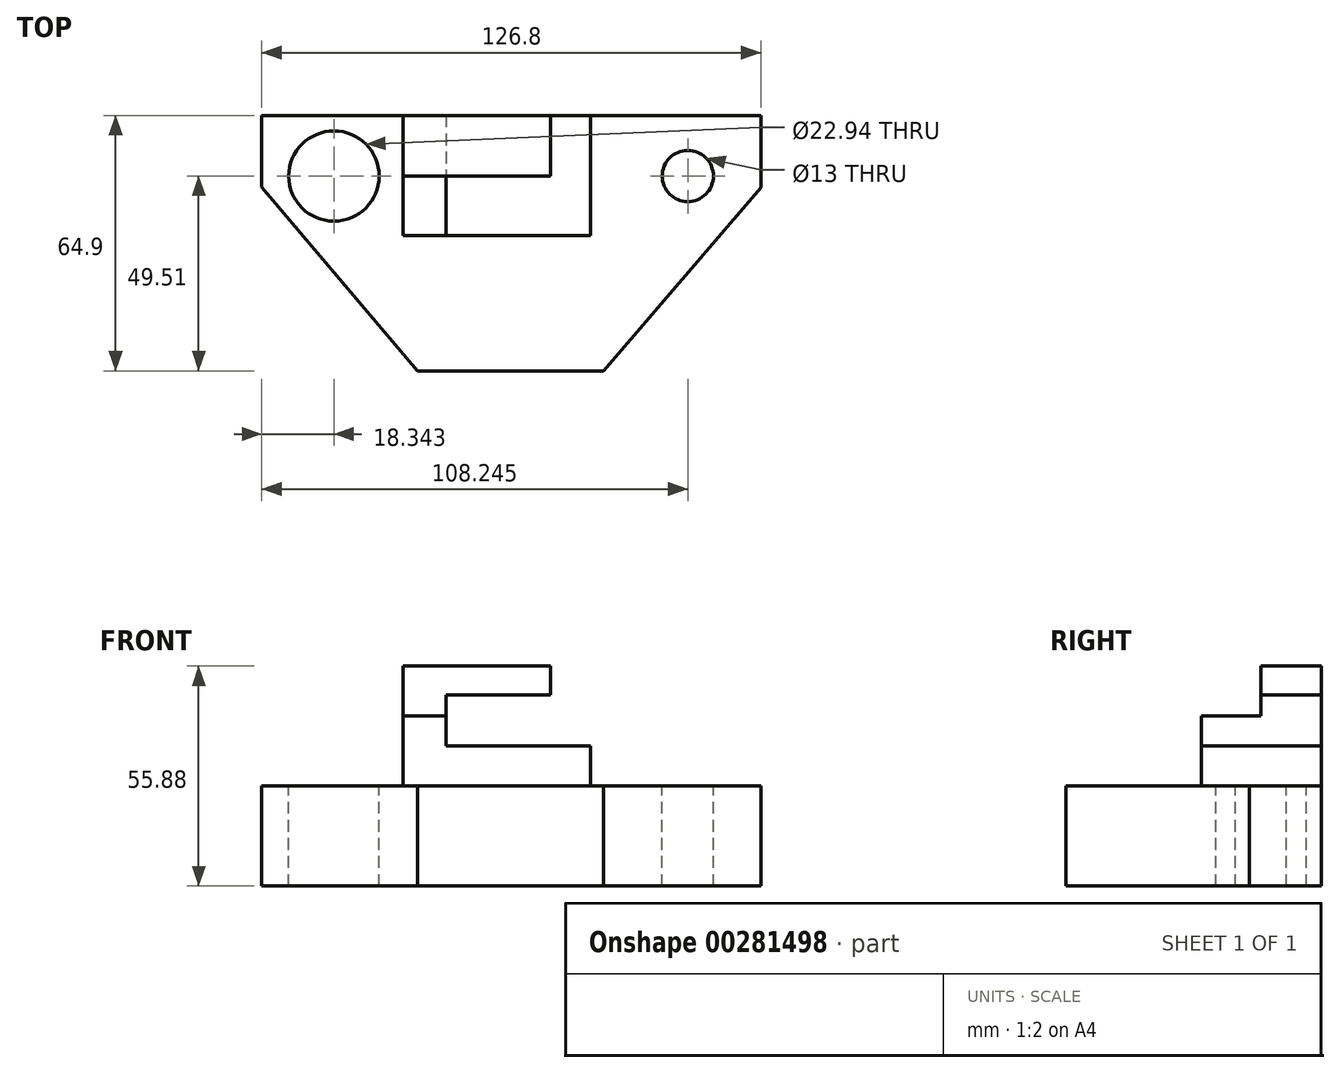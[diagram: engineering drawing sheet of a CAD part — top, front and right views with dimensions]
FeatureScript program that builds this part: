
annotation { "Feature Type Name" : "Feature", "Feature Type Description" : "" }
export const myFeature = defineFeature(function(context is Context, id is Id, definition is map)
    precondition{}
    {
        {
            var Q0;
            Q0=qCreatedBy(makeId("Top.planeOp"),FACE);
            var sketch = newSketch(context, id + "F0", { "sketchPlane" : qUnion([Q0])});
            skLineSegment(sketch, "E0.bottom", {"start": v(-62.57, 15.39) * mm, "end": v(64.23, 15.39) * mm});
            skLineSegment(sketch, "E0.top", {"start": v(-62.57, -49.51) * mm, "end": v(64.23, -49.51) * mm});
            skLineSegment(sketch, "E0.left", {"start": v(-62.57, 15.39) * mm, "end": v(-62.57, -49.51) * mm});
            skLineSegment(sketch, "E0.right", {"start": v(64.23, 15.39) * mm, "end": v(64.23, -49.51) * mm});
            skSolve(sketch);
        }
        {
            var Q0;
            Q0=makeQuery(id+"F0.imprint","IMPRINT",FACE,{"disambiguationData":[TD([[makeQuery(id+"F0.imprint","IMPRINT",EDGE,{"derivedFrom":sQuery(id+"F0.wireOp",EDGE,"E0.bottom")}),-1.0]])]});
            extrude(context, id + "F1", {"entities" : qUnion([Q0]), "depth" : 25.4 * mm});
        }
        {
            var Q0;
            Q0=makeQuery(id+"F1.opExtrude","CAP_FACE",FACE,{"disambiguationData":[OSD([sQuery(id+"F0.wireOp",EDGE,"E0.bottom"),sQuery(id+"F0.wireOp",EDGE,"E0.top"),sQuery(id+"F0.wireOp",EDGE,"E0.left"),sQuery(id+"F0.wireOp",EDGE,"E0.right")])],"isStart":false});
            var sketch = newSketch(context, id + "F2", { "sketchPlane" : qUnion([Q0])});
            skLineSegment(sketch, "E1", {"start": v(-62.57, -2.79) * mm, "end": v(-23.03, -49.51) * mm});
            skLineSegment(sketch, "E2", {"start": v(64.23, -2.99) * mm, "end": v(24.3, -49.51) * mm});
            skSolve(sketch);
        }
        {
            var Q0;
            {var subQ0=sQuery(id+"F2.wireOp",EDGE,"E1");Q0=makeQuery(id+"F2.imprint","IMPRINT",FACE,{"disambiguationData":[TD([[makeQuery(id+"F2.imprint","IMPRINT",EDGE,{"derivedFrom":subQ0}),-1.0]])]});}
            var Q1;
            {var subQ0=sQuery(id+"F2.wireOp",EDGE,"E2");Q1=makeQuery(id+"F2.imprint","IMPRINT",FACE,{"disambiguationData":[TD([[makeQuery(id+"F2.imprint","IMPRINT",EDGE,{"derivedFrom":subQ0}),1.0]])]});}
            extrude(context, id + "F3", {"entities" : qUnion([Q0, Q1]), "operationType" : NewBodyOperationType.REMOVE, "oppositeDirection" : true, "depth" : 25.4 * mm});
        }
        {
            var Q0;
            Q0=makeQuery(id+"F1.opExtrude","CAP_FACE",FACE,{"disambiguationData":[OSD([sQuery(id+"F0.wireOp",EDGE,"E0.bottom"),sQuery(id+"F0.wireOp",EDGE,"E0.top"),sQuery(id+"F0.wireOp",EDGE,"E0.left"),sQuery(id+"F0.wireOp",EDGE,"E0.right")])],"isStart":false});
            var sketch = newSketch(context, id + "F4", { "sketchPlane" : qUnion([Q0])});
            skLineSegment(sketch, "E3.bottom", {"start": v(-26.63, 15.39) * mm, "end": v(20.9, 15.39) * mm});
            skLineSegment(sketch, "E3.top", {"start": v(-26.63, -15.17) * mm, "end": v(20.9, -15.17) * mm});
            skLineSegment(sketch, "E3.left", {"start": v(-26.63, 15.39) * mm, "end": v(-26.63, -15.17) * mm});
            skLineSegment(sketch, "E3.right", {"start": v(20.9, 15.39) * mm, "end": v(20.9, -15.17) * mm});
            skSolve(sketch);
        }
        {
            var Q0;
            Q0=makeQuery(id+"F4.imprint","IMPRINT",FACE,{"disambiguationData":[TD([[makeQuery(id+"F4.imprint","IMPRINT",EDGE,{"derivedFrom":sQuery(id+"F4.wireOp",EDGE,"E3.bottom")}),-1.0]])]});
            extrude(context, id + "F5", {"entities" : qUnion([Q0]), "operationType" : NewBodyOperationType.ADD, "depth" : 10.16 * mm});
        }
        {
            var Q0;
            Q0=makeQuery(id+"F5.opExtrude","CAP_FACE",FACE,{"disambiguationData":[OSD([sQuery(id+"F4.wireOp",EDGE,"E3.bottom"),sQuery(id+"F4.wireOp",EDGE,"E3.top"),sQuery(id+"F4.wireOp",EDGE,"E3.left"),sQuery(id+"F4.wireOp",EDGE,"E3.right")])],"isStart":false});
            var sketch = newSketch(context, id + "F6", { "sketchPlane" : qUnion([Q0])});
            skLineSegment(sketch, "E4.bottom", {"start": v(-26.63, 15.39) * mm, "end": v(20.9, 15.39) * mm});
            skLineSegment(sketch, "E4.top", {"start": v(-26.63, 0) * mm, "end": v(20.9, 0) * mm});
            skLineSegment(sketch, "E4.left", {"start": v(-26.63, 15.39) * mm, "end": v(-26.63, 0) * mm});
            skLineSegment(sketch, "E4.right", {"start": v(20.9, 15.39) * mm, "end": v(20.9, 0) * mm});
            skSolve(sketch);
        }
        {
            var Q0;
            Q0=makeQuery(id+"F6.imprint","IMPRINT",FACE,{"disambiguationData":[TD([[makeQuery(id+"F6.imprint","IMPRINT",EDGE,{"derivedFrom":sQuery(id+"F6.wireOp",EDGE,"E4.bottom")}),-1.0]])]});
            extrude(context, id + "F7", {"entities" : qUnion([Q0]), "operationType" : NewBodyOperationType.ADD, "depth" : 20.32 * mm});
        }
        {
            var Q0;
            Q0=makeQuery(id+"F7.opExtrude","SWEPT_FACE",FACE,{"disambiguationData":[OSD([sQuery(id+"F6.wireOp",EDGE,"E4.top")])]});
            var sketch = newSketch(context, id + "F8", { "sketchPlane" : qUnion([Q0])});
            skLineSegment(sketch, "E5.bottom", {"start": v(-15.77, 35.56) * mm, "end": v(20.9, 35.56) * mm});
            skLineSegment(sketch, "E5.top", {"start": v(-15.77, 48.56) * mm, "end": v(20.9, 48.56) * mm});
            skLineSegment(sketch, "E5.left", {"start": v(-15.77, 35.56) * mm, "end": v(-15.77, 48.56) * mm});
            skLineSegment(sketch, "E5.right", {"start": v(20.9, 35.56) * mm, "end": v(20.9, 48.56) * mm});
            skSolve(sketch);
        }
        {
            var Q0;
            Q0=makeQuery(id+"F8.imprint","IMPRINT",FACE,{"disambiguationData":[TD([[makeQuery(id+"F8.imprint","IMPRINT",EDGE,{"derivedFrom":sQuery(id+"F8.wireOp",EDGE,"E5.bottom")}),1.0]])]});
            extrude(context, id + "F9", {"entities" : qUnion([Q0]), "operationType" : NewBodyOperationType.REMOVE, "oppositeDirection" : true, "depth" : 25.4 * mm});
        }
        {
            var Q0;
            Q0=makeQuery(id+"F7.opExtrude","CAP_FACE",FACE,{"disambiguationData":[OSD([sQuery(id+"F6.wireOp",EDGE,"E4.bottom"),sQuery(id+"F6.wireOp",EDGE,"E4.top"),sQuery(id+"F6.wireOp",EDGE,"E4.left"),sQuery(id+"F6.wireOp",EDGE,"E4.right")])],"isStart":false});
            var sketch = newSketch(context, id + "F10", { "sketchPlane" : qUnion([Q0])});
            skLineSegment(sketch, "E6.bottom", {"start": v(10.76, 15.39) * mm, "end": v(20.9, 15.39) * mm});
            skLineSegment(sketch, "E6.top", {"start": v(10.76, 0) * mm, "end": v(20.9, 0) * mm});
            skLineSegment(sketch, "E6.left", {"start": v(10.76, 15.39) * mm, "end": v(10.76, 0) * mm});
            skLineSegment(sketch, "E6.right", {"start": v(20.9, 15.39) * mm, "end": v(20.9, 0) * mm});
            skSolve(sketch);
        }
        {
            var Q0;
            Q0=makeQuery(id+"F10.imprint","IMPRINT",FACE,{"disambiguationData":[TD([[makeQuery(id+"F10.imprint","IMPRINT",EDGE,{"derivedFrom":sQuery(id+"F10.wireOp",EDGE,"E6.bottom")}),-1.0]])]});
            extrude(context, id + "F11", {"entities" : qUnion([Q0]), "operationType" : NewBodyOperationType.REMOVE, "oppositeDirection" : true, "depth" : 15.24 * mm});
        }
        {
            var Q0;
            Q0=makeQuery(id+"F9.boolean.opBoolean","MERGE",FACE,{"derivedFrom":[makeQuery(id+"F5.opExtrude","CAP_FACE",FACE,{"disambiguationData":[OSD([sQuery(id+"F4.wireOp",EDGE,"E3.bottom"),sQuery(id+"F4.wireOp",EDGE,"E3.top"),sQuery(id+"F4.wireOp",EDGE,"E3.left"),sQuery(id+"F4.wireOp",EDGE,"E3.right")])],"isStart":false}),makeQuery(id+"F9.opExtrude","SWEPT_FACE",FACE,{"disambiguationData":[OSD([sQuery(id+"F8.wireOp",EDGE,"E5.bottom")])]})]});
            var sketch = newSketch(context, id + "F12", { "sketchPlane" : qUnion([Q0])});
            skLineSegment(sketch, "E7.bottom", {"start": v(-26.63, 0) * mm, "end": v(-15.77, 0) * mm});
            skLineSegment(sketch, "E7.top", {"start": v(-26.63, -15.17) * mm, "end": v(-15.77, -15.17) * mm});
            skLineSegment(sketch, "E7.left", {"start": v(-26.63, 0) * mm, "end": v(-26.63, -15.17) * mm});
            skLineSegment(sketch, "E7.right", {"start": v(-15.77, 0) * mm, "end": v(-15.77, -15.17) * mm});
            skSolve(sketch);
        }
        {
            var Q0;
            Q0=makeQuery(id+"F12.imprint","IMPRINT",FACE,{"disambiguationData":[TD([[makeQuery(id+"F12.imprint","IMPRINT",EDGE,{"derivedFrom":sQuery(id+"F12.wireOp",EDGE,"E7.bottom")}),-1.0]])]});
            extrude(context, id + "F13", {"entities" : qUnion([Q0]), "operationType" : NewBodyOperationType.ADD, "depth" : 7.62 * mm});
        }
        {
            var Q0;
            Q0=makeQuery(id+"F1.opExtrude","CAP_FACE",FACE,{"disambiguationData":[OSD([sQuery(id+"F0.wireOp",EDGE,"E0.bottom"),sQuery(id+"F0.wireOp",EDGE,"E0.top"),sQuery(id+"F0.wireOp",EDGE,"E0.left"),sQuery(id+"F0.wireOp",EDGE,"E0.right")])],"isStart":false});
            var sketch = newSketch(context, id + "F14", { "sketchPlane" : qUnion([Q0])});
            skLineSegment(sketch, "E8", {"start": v(-44.23, 0) * mm, "end": v(-42.34, 15.39) * mm});
            skLineSegment(sketch, "E9", {"start": v(-44.23, 0) * mm, "end": v(-60.7, 2.02) * mm});
            skLineSegment(sketch, "E10", {"start": v(-44.23, 0) * mm, "end": v(-44.23, -19.5) * mm});
            skLineSegment(sketch, "E11", {"start": v(-44.23, 0) * mm, "end": v(-26.63, -2.16) * mm});
            skCircle(sketch, "E12", {"center": v(-44.23, 0) * mm, "radius": 11.47 * mm});
            skSolve(sketch);
        }
        {
            var Q0;
            {var subQ0=sQuery(id+"F14.wireOp",EDGE,"E9");var subQ3=sQuery(id+"F14.wireOp",EDGE,"E12");var subQ5=makeQuery(id+"F14.imprint","INTERSECT",VERTEX,{"derivedFrom":[subQ0,subQ3]});Q0=makeQuery(id+"F14.imprint","IMPRINT",FACE,{"disambiguationData":[TD([[makeQuery(id+"F14.imprint","IMPRINT",EDGE,{"disambiguationData":[TD([[subQ5,1.0]])],"derivedFrom":subQ3}),1.0]])]});}
            var Q1;
            {var subQ1=sQuery(id+"F14.wireOp",EDGE,"E9");var subQ3=sQuery(id+"F14.wireOp",EDGE,"E12");var subQ4=makeQuery(id+"F14.imprint","INTERSECT",VERTEX,{"derivedFrom":[subQ1,subQ3]});Q1=makeQuery(id+"F14.imprint","IMPRINT",FACE,{"disambiguationData":[TD([[makeQuery(id+"F14.imprint","IMPRINT",EDGE,{"disambiguationData":[TD([[subQ4,-1.0]])],"derivedFrom":subQ3}),1.0]])]});}
            var Q2;
            {var subQ1=sQuery(id+"F14.wireOp",EDGE,"E10");var subQ3=sQuery(id+"F14.wireOp",EDGE,"E12");var subQ4=makeQuery(id+"F14.imprint","INTERSECT",VERTEX,{"derivedFrom":[subQ1,subQ3]});Q2=makeQuery(id+"F14.imprint","IMPRINT",FACE,{"disambiguationData":[TD([[makeQuery(id+"F14.imprint","IMPRINT",EDGE,{"disambiguationData":[TD([[subQ4,-1.0]])],"derivedFrom":subQ3}),1.0]])]});}
            var Q3;
            {var subQ1=sQuery(id+"F14.wireOp",EDGE,"E8");var subQ3=sQuery(id+"F14.wireOp",EDGE,"E12");var subQ4=makeQuery(id+"F14.imprint","INTERSECT",VERTEX,{"derivedFrom":[subQ1,subQ3]});Q3=makeQuery(id+"F14.imprint","IMPRINT",FACE,{"disambiguationData":[TD([[makeQuery(id+"F14.imprint","IMPRINT",EDGE,{"disambiguationData":[TD([[subQ4,1.0]])],"derivedFrom":subQ3}),1.0]])]});}
            extrude(context, id + "F15", {"entities" : qUnion([Q0, Q1, Q2, Q3]), "operationType" : NewBodyOperationType.REMOVE, "oppositeDirection" : true, "depth" : 43.18 * mm});
        }
        {
            var Q0;
            Q0=makeQuery(id+"F1.opExtrude","CAP_FACE",FACE,{"disambiguationData":[OSD([sQuery(id+"F0.wireOp",EDGE,"E0.bottom"),sQuery(id+"F0.wireOp",EDGE,"E0.top"),sQuery(id+"F0.wireOp",EDGE,"E0.left"),sQuery(id+"F0.wireOp",EDGE,"E0.right")])],"isStart":false});
            var sketch = newSketch(context, id + "F16", { "sketchPlane" : qUnion([Q0])});
            skLineSegment(sketch, "E13", {"start": v(45.68, 0) * mm, "end": v(43.98, 17.83) * mm});
            skLineSegment(sketch, "E14", {"start": v(45.68, 0) * mm, "end": v(37.25, -0.8) * mm});
            skLineSegment(sketch, "E15", {"start": v(45.68, 0) * mm, "end": v(56.98, 4.77) * mm});
            skLineSegment(sketch, "E16", {"start": v(45.68, 0) * mm, "end": v(46.71, -10.88) * mm});
            skCircle(sketch, "E17", {"center": v(45.68, 0) * mm, "radius": 6.5 * mm});
            skSolve(sketch);
        }
        {
            var Q0;
            {var subQ1=sQuery(id+"F16.wireOp",EDGE,"E13");var subQ3=sQuery(id+"F16.wireOp",EDGE,"E17");var subQ4=makeQuery(id+"F16.imprint","INTERSECT",VERTEX,{"derivedFrom":[subQ1,subQ3]});Q0=makeQuery(id+"F16.imprint","IMPRINT",FACE,{"disambiguationData":[TD([[makeQuery(id+"F16.imprint","IMPRINT",EDGE,{"disambiguationData":[TD([[subQ4,-1.0]])],"derivedFrom":subQ3}),1.0]])]});}
            var Q1;
            {var subQ1=sQuery(id+"F16.wireOp",EDGE,"E13");var subQ3=sQuery(id+"F16.wireOp",EDGE,"E17");var subQ4=makeQuery(id+"F16.imprint","INTERSECT",VERTEX,{"derivedFrom":[subQ1,subQ3]});Q1=makeQuery(id+"F16.imprint","IMPRINT",FACE,{"disambiguationData":[TD([[makeQuery(id+"F16.imprint","IMPRINT",EDGE,{"disambiguationData":[TD([[subQ4,1.0]])],"derivedFrom":subQ3}),1.0]])]});}
            var Q2;
            {var subQ1=sQuery(id+"F16.wireOp",EDGE,"E15");var subQ3=sQuery(id+"F16.wireOp",EDGE,"E17");var subQ4=makeQuery(id+"F16.imprint","INTERSECT",VERTEX,{"derivedFrom":[subQ1,subQ3]});Q2=makeQuery(id+"F16.imprint","IMPRINT",FACE,{"disambiguationData":[TD([[makeQuery(id+"F16.imprint","IMPRINT",EDGE,{"disambiguationData":[TD([[subQ4,1.0]])],"derivedFrom":subQ3}),1.0]])]});}
            var Q3;
            {var subQ1=sQuery(id+"F16.wireOp",EDGE,"E14");var subQ3=sQuery(id+"F16.wireOp",EDGE,"E17");var subQ4=makeQuery(id+"F16.imprint","INTERSECT",VERTEX,{"derivedFrom":[subQ1,subQ3]});Q3=makeQuery(id+"F16.imprint","IMPRINT",FACE,{"disambiguationData":[TD([[makeQuery(id+"F16.imprint","IMPRINT",EDGE,{"disambiguationData":[TD([[subQ4,-1.0]])],"derivedFrom":subQ3}),1.0]])]});}
            extrude(context, id + "F17", {"entities" : qUnion([Q0, Q1, Q2, Q3]), "operationType" : NewBodyOperationType.REMOVE, "oppositeDirection" : true, "depth" : 50.8 * mm});
        }
    });
